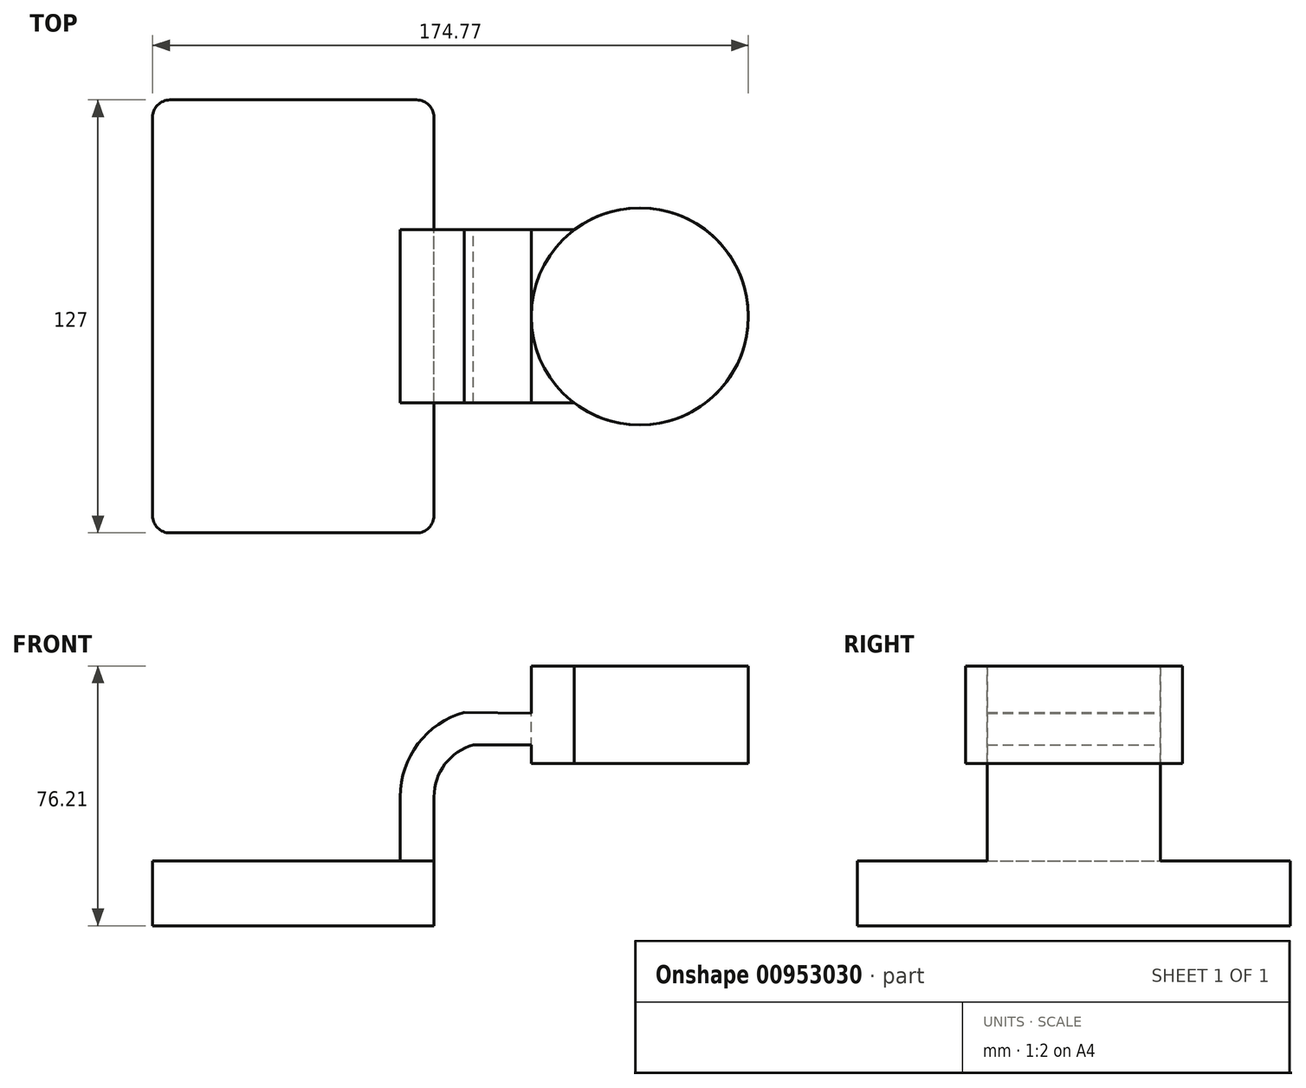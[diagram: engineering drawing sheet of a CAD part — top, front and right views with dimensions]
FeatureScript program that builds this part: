
annotation { "Feature Type Name" : "Feature", "Feature Type Description" : "" }
export const myFeature = defineFeature(function(context is Context, id is Id, definition is map)
    precondition{}
    {
        {
            var Q0;
            Q0=qCreatedBy(makeId("Front.planeOp"),FACE);
            var sketch = newSketch(context, id + "F0", { "sketchPlane" : qUnion([Q0])});
            skLineSegment(sketch, "E0.bottom", {"start": v(41.28, 9.53) * mm, "end": v(-41.28, 9.53) * mm});
            skLineSegment(sketch, "E0.top", {"start": v(41.28, -9.52) * mm, "end": v(-41.28, -9.52) * mm});
            skLineSegment(sketch, "E0.left", {"start": v(41.28, 9.53) * mm, "end": v(41.28, -9.52) * mm});
            skLineSegment(sketch, "E0.right", {"start": v(-41.28, 9.53) * mm, "end": v(-41.28, -9.52) * mm});
            skPoint(sketch, "E0.middle", {"position": v(0, 0) * mm});
            skLineSegment(sketch, "E1.bottom", {"start": v(101.65, 66.68) * mm, "end": v(69.8, 66.68) * mm});
            skLineSegment(sketch, "E1.top", {"start": v(101.65, 38.1) * mm, "end": v(69.8, 38.1) * mm});
            skLineSegment(sketch, "E1.left", {"start": v(101.65, 66.67) * mm, "end": v(101.65, 38.1) * mm});
            skLineSegment(sketch, "E1.right", {"start": v(69.8, 66.67) * mm, "end": v(69.8, 38.1) * mm});
            skPoint(sketch, "E1.middle", {"position": v(85.73, 52.39) * mm});
            skLineSegment(sketch, "E2", {"start": v(41.28, 9.53) * mm, "end": v(41.28, 28.27) * mm});
            skArc(sketch, "E3", {"start": v(41.28, 28.27) * mm, "mid": v(44.5, 37.86) * mm, "end": v(52.85, 43.55) * mm});
            skLineSegment(sketch, "E4", {"start": v(52.85, 43.55) * mm, "end": v(74.66, 43.55) * mm});
            skArc(sketch, "E5.0", {"start": v(31.37, 28.27) * mm, "mid": v(36.6, 43.84) * mm, "end": v(50.17, 53.09) * mm});
            skLineSegment(sketch, "E6", {"start": v(31.37, 28.27) * mm, "end": v(31.37, 9.53) * mm});
            skLineSegment(sketch, "E7", {"start": v(50.17, 53.09) * mm, "end": v(91.4, 52.39) * mm});
            skFitSpline(sketch, "E8", {"points": [v(-41.28, 9.53) * mm, v(54.7, 66.42) * mm, v(69.8, 66.68) * mm], "startDerivative": vector(122.54, 142.05) * mm, "endDerivative": vector(37.56, 0.34) * mm});
            skFitSpline(sketch, "E9", {"points": [v(-11.42, 44.14) * mm, v(0.6, 44.26) * mm], "startDerivative": vector(5, 2.71) * mm, "endDerivative": vector(-43.7, 0.64) * mm});
            skSolve(sketch);
        }
        {
            var Q0;
            Q0=makeQuery(id+"F0.imprint","IMPRINT",FACE,{"disambiguationData":[TD([[makeQuery(id+"F0.imprint","IMPRINT",EDGE,{"derivedFrom":sQuery(id+"F0.wireOp",EDGE,"E0.top")}),-1.0]])]});
            extrude(context, id + "F1", {"entities" : qUnion([Q0]), "endBound" : BoundingType.SYMMETRIC, "depth" : 127 * mm, "offsetDistance" : 25.4 * mm});
        }
        {
            var Q0;
            {var subQ1=sQuery(id+"F0.wireOp",EDGE,"E2");Q0=makeQuery(id+"F0.imprint","IMPRINT",FACE,{"disambiguationData":[TD([[makeQuery(id+"F0.imprint","IMPRINT",EDGE,{"derivedFrom":subQ1}),1.0]])]});}
            var Q1;
            {var subQ1=sQuery(id+"F0.wireOp",EDGE,"E1.bottom");Q1=makeQuery(id+"F0.imprint","IMPRINT",FACE,{"disambiguationData":[TD([[makeQuery(id+"F0.imprint","IMPRINT",EDGE,{"derivedFrom":subQ1}),1.0]])]});}
            extrude(context, id + "F2", {"entities" : qUnion([Q0, Q1]), "operationType" : NewBodyOperationType.ADD, "endBound" : BoundingType.SYMMETRIC, "depth" : 50.8 * mm, "offsetDistance" : 25.4 * mm});
        }
        {
            var Q0;
            {var subQ1=sQuery(id+"F0.wireOp",EDGE,"E5.0");Q0=makeQuery(id+"F0.imprint","IMPRINT",FACE,{"disambiguationData":[TD([[makeQuery(id+"F0.imprint","IMPRINT",EDGE,{"derivedFrom":subQ1}),1.0]])]});}
            extrude(context, id + "F3", {"entities" : qUnion([Q0]), "operationType" : NewBodyOperationType.ADD, "endBound" : BoundingType.SYMMETRIC, "depth" : 15.88 * mm, "offsetDistance" : 25.4 * mm});
        }
        {
            var Q0;
            {var subQ1=sQuery(id+"F0.wireOp",EDGE,"E1.bottom");Q0=makeQuery(id+"F0.imprint","IMPRINT",FACE,{"disambiguationData":[TD([[makeQuery(id+"F0.imprint","IMPRINT",EDGE,{"derivedFrom":subQ1}),1.0]])]});}
            var Q1;
            Q1=sQuery(id+"F0.wireOp",EDGE,"E1.left");
            revolve(context, id + "F4", {"surfaceOperationType" : NewSurfaceOperationType.NEW, "entities" : qUnion([Q0]), "axis" : qUnion([Q1]), "revolveType" : RevolveType.FULL});
        }
        {
            var Q0;
            Q0=makeQuery(id+"F1.opExtrude","CAP_EDGE",EDGE,{"disambiguationData":[OSD([sQuery(id+"F0.wireOp",EDGE,"E0.right")])],"isStart":false});
            var Q1;
            Q1=makeQuery(id+"F1.opExtrude","CAP_EDGE",EDGE,{"disambiguationData":[OSD([sQuery(id+"F0.wireOp",EDGE,"E0.left")])],"isStart":false});
            var Q2;
            Q2=makeQuery(id+"F1.opExtrude","CAP_EDGE",EDGE,{"disambiguationData":[OSD([sQuery(id+"F0.wireOp",EDGE,"E0.right")])],"isStart":true});
            var Q3;
            Q3=makeQuery(id+"F1.opExtrude","CAP_EDGE",EDGE,{"disambiguationData":[OSD([sQuery(id+"F0.wireOp",EDGE,"E0.left")])],"isStart":true});
            fillet(context, id + "F5", {"entities" : qUnion([Q0, Q1, Q2, Q3]), "radius" : 5.08 * mm, "tangentPropagation" : true, "allowEdgeOverflow" : false});
        }
    });
